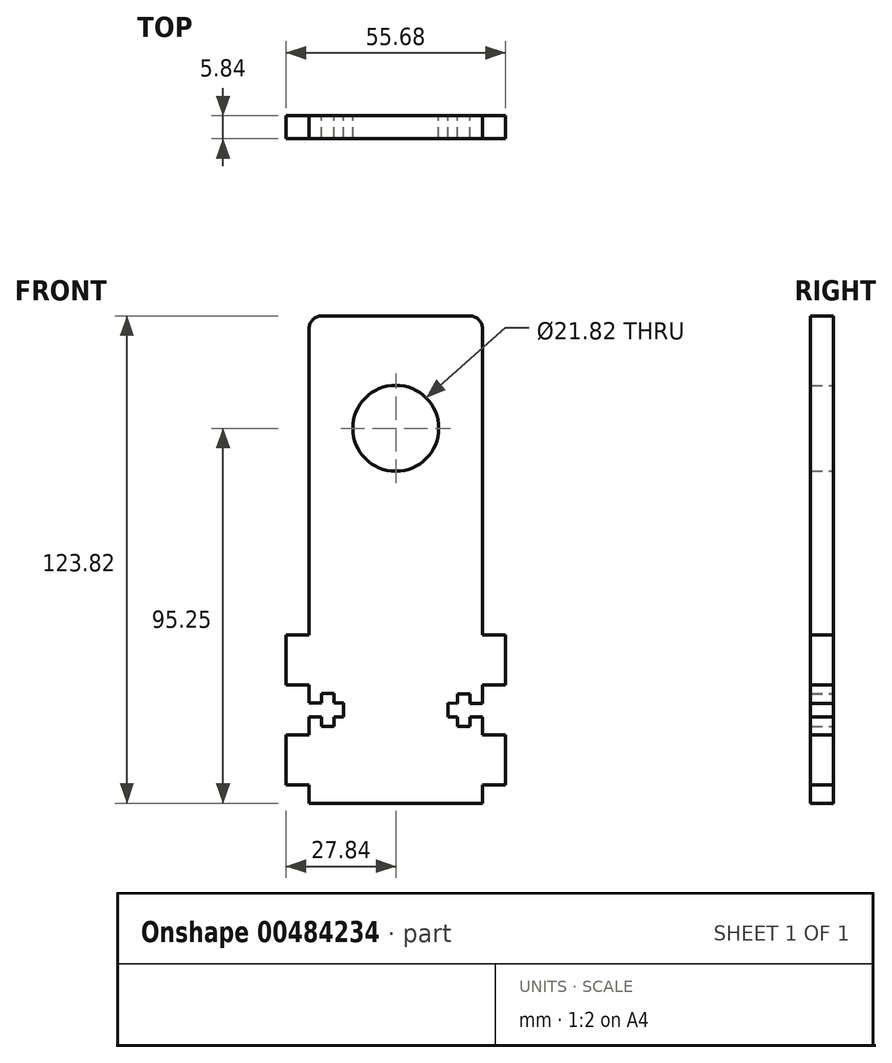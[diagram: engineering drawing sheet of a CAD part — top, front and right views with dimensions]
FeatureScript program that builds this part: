
annotation { "Feature Type Name" : "Feature", "Feature Type Description" : "" }
export const myFeature = defineFeature(function(context is Context, id is Id, definition is map)
    precondition{}
    {
        {
            var Q0;
            Q0=qCreatedBy(makeId("Front.planeOp"),FACE);
            var sketch = newSketch(context, id + "F0", { "sketchPlane" : qUnion([Q0])});
            skCircle(sketch, "E0", {"center": v(0, 0) * mm, "radius": 10.91 * mm});
            skCircle(sketch, "E1", {"center": v(0, 0) * mm, "radius": 8 * mm, "construction": true});
            skArc(sketch, "E2", {"start": v(-7.5, -71.55) * mm, "mid": v(-7.49, -72) * mm, "end": v(-7.45, -72.43) * mm});
            skLineSegment(sketch, "E3.bottom", {"start": v(-22, 28.58) * mm, "end": v(22, 28.58) * mm});
            skLineSegment(sketch, "E3.top", {"start": v(-22, -95.25) * mm, "end": v(22, -95.25) * mm});
            skLineSegment(sketch, "E3.right", {"start": v(22, 28.58) * mm, "end": v(22, -52.5) * mm});
            skPoint(sketch, "E3.middle", {"position": v(0, -33.34) * mm});
            skCircle(sketch, "E4", {"center": v(0, 0) * mm, "radius": 15.88 * mm, "construction": true});
            skLineSegment(sketch, "E5.bottom", {"start": v(-21.15, -50.4) * mm, "end": v(21.15, -50.4) * mm, "construction": true});
            skLineSegment(sketch, "E5.top", {"start": v(-21.15, -92.7) * mm, "end": v(21.15, -92.7) * mm, "construction": true});
            skLineSegment(sketch, "E5.left", {"start": v(-21.15, -50.4) * mm, "end": v(-21.15, -92.7) * mm, "construction": true});
            skLineSegment(sketch, "E5.right", {"start": v(21.15, -50.4) * mm, "end": v(21.15, -92.7) * mm, "construction": true});
            skLineSegment(sketch, "E6", {"start": v(-15.77, -1.86) * mm, "end": v(-7.45, -72.43) * mm, "construction": true});
            skLineSegment(sketch, "E7", {"start": v(0, 0) * mm, "end": v(0, -71.55) * mm, "construction": true});
            skLineSegment(sketch, "E8.MirrorCS", {"start": v(15.77, -1.86) * mm, "end": v(7.45, -72.43) * mm, "construction": true});
            skLineSegment(sketch, "E9", {"start": v(-21.15, -71.55) * mm, "end": v(21.15, -71.55) * mm, "construction": true});
            skLineSegment(sketch, "E10", {"start": v(0, -92.7) * mm, "end": v(0, -50.4) * mm, "construction": true});
            skLineSegment(sketch, "E11.bottom", {"start": v(-22, -77.9) * mm, "end": v(-27.84, -77.9) * mm});
            skLineSegment(sketch, "E11.top", {"start": v(-22, -90.6) * mm, "end": v(-27.84, -90.6) * mm});
            skLineSegment(sketch, "E11.right", {"start": v(-27.84, -77.9) * mm, "end": v(-27.84, -90.6) * mm});
            skPoint(sketch, "E11.middle", {"position": v(-24.92, -84.25) * mm});
            skLineSegment(sketch, "E12.MirrorCS", {"start": v(-22, -65.2) * mm, "end": v(-27.84, -65.2) * mm});
            skLineSegment(sketch, "E13.MirrorCS", {"start": v(-27.84, -65.2) * mm, "end": v(-27.84, -52.5) * mm});
            skLineSegment(sketch, "E14.MirrorCS", {"start": v(-22, -52.5) * mm, "end": v(-27.84, -52.5) * mm});
            skLineSegment(sketch, "E15.trimOffspring", {"start": v(-22, -65.2) * mm, "end": v(-22, -77.9) * mm});
            skLineSegment(sketch, "E16.trimOffspring", {"start": v(-22, -90.6) * mm, "end": v(-22, -95.25) * mm});
            skLineSegment(sketch, "E17", {"start": v(-22, -52.5) * mm, "end": v(-22, 28.58) * mm});
            skPoint(sketch, "E18.middle", {"position": v(-12.7, 22.23) * mm});
            skLineSegment(sketch, "E19.MirrorCS", {"start": v(22, -52.5) * mm, "end": v(27.84, -52.5) * mm});
            skLineSegment(sketch, "E20.MirrorCS", {"start": v(27.84, -65.2) * mm, "end": v(27.84, -52.5) * mm});
            skLineSegment(sketch, "E21.MirrorCS", {"start": v(22, -77.9) * mm, "end": v(27.84, -77.9) * mm});
            skLineSegment(sketch, "E22.MirrorCS", {"start": v(27.84, -77.9) * mm, "end": v(27.84, -90.6) * mm});
            skLineSegment(sketch, "E23.MirrorCS", {"start": v(22, -90.6) * mm, "end": v(27.84, -90.6) * mm});
            skLineSegment(sketch, "E24", {"start": v(27.84, -65.2) * mm, "end": v(22, -65.2) * mm});
            skLineSegment(sketch, "E25.trimOffspring", {"start": v(22, -65.2) * mm, "end": v(22, -77.9) * mm});
            skLineSegment(sketch, "E26.trimOffspring", {"start": v(22, -90.6) * mm, "end": v(22, -95.25) * mm});
            skLineSegment(sketch, "E27", {"start": v(0, -33.34) * mm, "end": v(22, -33.34) * mm, "construction": true});
            skLineSegment(sketch, "E28", {"start": v(0, -33.34) * mm, "end": v(-22, -33.34) * mm, "construction": true});
            skPoint(sketch, "E29", {"position": v(-12.06, -33.34) * mm});
            skArc(sketch, "E30.trimOffspring", {"start": v(7.45, -72.43) * mm, "mid": v(7.49, -72) * mm, "end": v(7.5, -71.55) * mm});
            skPoint(sketch, "E31.center.orphan", {"position": v(-15.5, -56.05) * mm});
            skPoint(sketch, "E32.center.orphan", {"position": v(-12.26, -33.34) * mm});
            skPoint(sketch, "E33.MirrorCS.end.orphan", {"position": v(6.35, 19.3) * mm});
            skPoint(sketch, "E33.MirrorCS.start.orphan", {"position": v(6.35, 25.15) * mm});
            skPoint(sketch, "E34.MirrorCS.end.orphan", {"position": v(19.05, 25.15) * mm});
            skPoint(sketch, "E35.MirrorCS.end.orphan", {"position": v(19.05, 19.3) * mm});
            skPoint(sketch, "E18.left.end.orphan", {"position": v(-6.35, 19.3) * mm});
            skPoint(sketch, "E18.left.start.orphan", {"position": v(-6.35, 25.15) * mm});
            skPoint(sketch, "E18.right.end.orphan", {"position": v(-19.05, 19.3) * mm});
            skPoint(sketch, "E18.right.start.orphan", {"position": v(-19.05, 25.15) * mm});
            skSolve(sketch);
        }
        {
            var Q0;
            Q0=qSketchRegion(id+"F0",true);
            extrude(context, id + "F1", {"entities" : qUnion([Q0]), "depth" : 5.84 * mm});
        }
        {
            var Q0;
            Q0=makeQuery(id+"F1.opExtrude","SWEPT_EDGE",EDGE,{"disambiguationData":[OSD([sQuery(id+"F0.wireOp",EDGE,"E3.bottom"),sQuery(id+"F0.wireOp",EDGE,"E3.right")])]});
            var Q1;
            Q1=makeQuery(id+"F1.opExtrude","SWEPT_EDGE",EDGE,{"disambiguationData":[OSD([sQuery(id+"F0.wireOp",EDGE,"E3.bottom"),sQuery(id+"F0.wireOp",EDGE,"E17")])]});
            fillet(context, id + "F2", {"entities" : qUnion([Q0, Q1]), "radius" : 3.17 * mm, "tangentPropagation" : true, "allowEdgeOverflow" : false});
        }
        {
            var Q0;
            Q0=makeQuery(id+"F1.opExtrude","CAP_FACE",FACE,{"disambiguationData":[OSD([sQuery(id+"F0.wireOp",EDGE,"E0"),sQuery(id+"F0.wireOp",EDGE,"E3.bottom"),sQuery(id+"F0.wireOp",EDGE,"E3.top"),sQuery(id+"F0.wireOp",EDGE,"E3.right"),sQuery(id+"F0.wireOp",EDGE,"E11.bottom"),sQuery(id+"F0.wireOp",EDGE,"E11.top"),sQuery(id+"F0.wireOp",EDGE,"E11.right"),sQuery(id+"F0.wireOp",EDGE,"E12.MirrorCS"),sQuery(id+"F0.wireOp",EDGE,"E13.MirrorCS"),sQuery(id+"F0.wireOp",EDGE,"E14.MirrorCS"),sQuery(id+"F0.wireOp",EDGE,"E15.trimOffspring"),sQuery(id+"F0.wireOp",EDGE,"E16.trimOffspring"),sQuery(id+"F0.wireOp",EDGE,"E17"),sQuery(id+"F0.wireOp",EDGE,"E19.MirrorCS"),sQuery(id+"F0.wireOp",EDGE,"E20.MirrorCS"),sQuery(id+"F0.wireOp",EDGE,"E21.MirrorCS"),sQuery(id+"F0.wireOp",EDGE,"E22.MirrorCS"),sQuery(id+"F0.wireOp",EDGE,"E23.MirrorCS"),sQuery(id+"F0.wireOp",EDGE,"E24"),sQuery(id+"F0.wireOp",EDGE,"E25.trimOffspring"),sQuery(id+"F0.wireOp",EDGE,"E26.trimOffspring")])],"isStart":true});
            var sketch = newSketch(context, id + "F3", { "sketchPlane" : qUnion([Q0])});
            skLineSegment(sketch, "E36", {"start": v(22, -71.55) * mm, "end": v(-22, -71.55) * mm, "construction": true});
            skLineSegment(sketch, "E37", {"start": v(0, -71.55) * mm, "end": v(0, -71.55) * mm});
            skPoint(sketch, "E37.endSnap0", {"position": v(0, -71.55) * mm});
            skLineSegment(sketch, "E38.bottom", {"start": v(22, -69.8) * mm, "end": v(18.83, -69.8) * mm});
            skLineSegment(sketch, "E38.top", {"start": v(22, -73.3) * mm, "end": v(18.83, -73.3) * mm});
            skLineSegment(sketch, "E38.left", {"start": v(22, -69.8) * mm, "end": v(22, -73.3) * mm});
            skPoint(sketch, "E38.middle", {"position": v(20.41, -71.55) * mm});
            skPoint(sketch, "E39.middle", {"position": v(17.24, -71.55) * mm});
            skLineSegment(sketch, "E40.bottom", {"start": v(15.65, -69.8) * mm, "end": v(13.27, -69.8) * mm});
            skLineSegment(sketch, "E40.top", {"start": v(15.65, -73.3) * mm, "end": v(13.27, -73.3) * mm});
            skLineSegment(sketch, "E40.right", {"start": v(13.27, -69.8) * mm, "end": v(13.27, -73.3) * mm});
            skPoint(sketch, "E40.middle", {"position": v(14.46, -71.55) * mm});
            skLineSegment(sketch, "E41.bottom", {"start": v(18.83, -67.4) * mm, "end": v(15.65, -67.4) * mm});
            skLineSegment(sketch, "E41.top", {"start": v(18.83, -75.71) * mm, "end": v(15.65, -75.71) * mm});
            skLineSegment(sketch, "E41.right", {"start": v(15.65, -67.4) * mm, "end": v(15.65, -69.8) * mm});
            skLineSegment(sketch, "E42.trimOffspring", {"start": v(18.83, -73.3) * mm, "end": v(18.83, -75.71) * mm});
            skLineSegment(sketch, "E43", {"start": v(18.83, -69.8) * mm, "end": v(18.83, -67.4) * mm});
            skLineSegment(sketch, "E44", {"start": v(15.65, -73.3) * mm, "end": v(15.65, -75.71) * mm});
            skLineSegment(sketch, "E45.MirrorCS", {"start": v(-15.64, -73.35) * mm, "end": v(-13.26, -73.35) * mm});
            skLineSegment(sketch, "E46.MirrorCS", {"start": v(-15.65, -69.85) * mm, "end": v(-13.27, -69.84) * mm});
            skLineSegment(sketch, "E47.MirrorCS", {"start": v(-15.66, -67.44) * mm, "end": v(-15.65, -69.85) * mm});
            skPoint(sketch, "E48.MirrorP", {"position": v(-17.24, -71.6) * mm});
            skLineSegment(sketch, "E49.MirrorCS", {"start": v(-15.64, -73.35) * mm, "end": v(-15.63, -75.76) * mm});
            skLineSegment(sketch, "E50.MirrorCS", {"start": v(-18.82, -73.36) * mm, "end": v(-18.81, -75.77) * mm});
            skLineSegment(sketch, "E51.MirrorCS", {"start": v(-22, -73.37) * mm, "end": v(-18.82, -73.36) * mm});
            skPoint(sketch, "E52.MirrorP", {"position": v(-20.41, -71.61) * mm});
            skLineSegment(sketch, "E53.MirrorCS", {"start": v(-18.81, -75.77) * mm, "end": v(-15.63, -75.76) * mm});
            skLineSegment(sketch, "E54.MirrorCS", {"start": v(-18.83, -69.86) * mm, "end": v(-18.84, -67.45) * mm});
            skLineSegment(sketch, "E55.MirrorCS", {"start": v(-18.84, -67.45) * mm, "end": v(-15.66, -67.44) * mm});
            skPoint(sketch, "E56.MirrorP", {"position": v(-14.46, -71.6) * mm});
            skLineSegment(sketch, "E57.MirrorCS", {"start": v(-22, -69.87) * mm, "end": v(-22, -73.37) * mm});
            skLineSegment(sketch, "E58.MirrorCS", {"start": v(-13.27, -69.84) * mm, "end": v(-13.26, -73.35) * mm});
            skLineSegment(sketch, "E59.MirrorCS", {"start": v(-22, -69.87) * mm, "end": v(-18.83, -69.86) * mm});
            skSolve(sketch);
        }
        {
            var Q0;
            Q0 = qSketchRegion(id + "F3", true);
            extrude(context, id + "F4", {"entities" : qUnion([Q0]), "operationType" : NewBodyOperationType.REMOVE, "oppositeDirection" : true, "depth" : 25.4 * mm});
        }
    });
